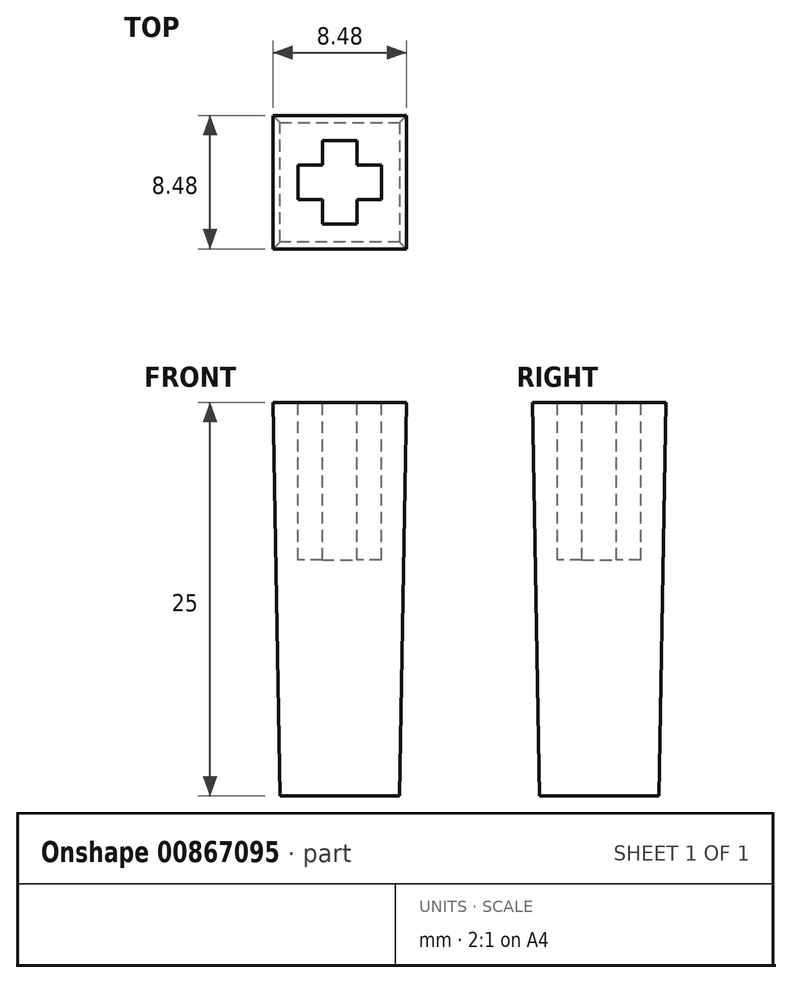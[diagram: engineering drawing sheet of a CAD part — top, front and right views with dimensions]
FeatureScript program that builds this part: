
annotation { "Feature Type Name" : "Feature", "Feature Type Description" : "" }
export const myFeature = defineFeature(function(context is Context, id is Id, definition is map)
    precondition{}
    {
        {
            var Q0;
            Q0=qCreatedBy(makeId("Top.planeOp"),FACE);
            var sketch = newSketch(context, id + "F0", { "sketchPlane" : qUnion([Q0])});
            skLineSegment(sketch, "E0.bottom", {"start": v(3.8, 3.8) * mm, "end": v(-3.8, 3.8) * mm});
            skLineSegment(sketch, "E0.top", {"start": v(3.8, -3.8) * mm, "end": v(-3.8, -3.8) * mm});
            skLineSegment(sketch, "E0.left", {"start": v(3.8, 3.8) * mm, "end": v(3.8, -3.8) * mm});
            skLineSegment(sketch, "E0.right", {"start": v(-3.8, 3.8) * mm, "end": v(-3.8, -3.8) * mm});
            skPoint(sketch, "E0.middle", {"position": v(0, 0) * mm});
            skSolve(sketch);
        }
        {
            var Q0;
            Q0 = qSketchRegion(id + "F0", true);
            extrude(context, id + "F1", {"entities" : qUnion([Q0]), "depth" : 25 * mm, "offsetDistance" : 25 * mm, "hasDraft" : true, "draftAngle" : 1 * degree});
        }
        {
            var Q0;
            Q0=makeQuery(id+"F1.opExtrude","CAP_FACE",FACE,{"disambiguationData":[OSD([sQuery(id+"F0.wireOp",EDGE,"E0.bottom"),sQuery(id+"F0.wireOp",EDGE,"E0.top"),sQuery(id+"F0.wireOp",EDGE,"E0.left"),sQuery(id+"F0.wireOp",EDGE,"E0.right")])],"isStart":false});
            var sketch = newSketch(context, id + "F2", { "sketchPlane" : qUnion([Q0])});
            skLineSegment(sketch, "E1.bottom", {"start": v(2.65, -1.1) * mm, "end": v(-2.65, -1.1) * mm});
            skLineSegment(sketch, "E1.top", {"start": v(2.65, 1.1) * mm, "end": v(-2.65, 1.1) * mm});
            skLineSegment(sketch, "E1.left", {"start": v(2.65, -1.1) * mm, "end": v(2.65, 1.1) * mm});
            skLineSegment(sketch, "E1.right", {"start": v(-2.65, -1.1) * mm, "end": v(-2.65, 1.1) * mm});
            skPoint(sketch, "E1.middle", {"position": v(0, 0) * mm});
            skLineSegment(sketch, "E2.bottom", {"start": v(-1.1, 2.65) * mm, "end": v(1.1, 2.65) * mm});
            skLineSegment(sketch, "E2.top", {"start": v(-1.1, -2.65) * mm, "end": v(1.1, -2.65) * mm});
            skLineSegment(sketch, "E2.left", {"start": v(-1.1, 2.65) * mm, "end": v(-1.1, -2.65) * mm});
            skLineSegment(sketch, "E2.right", {"start": v(1.1, 2.65) * mm, "end": v(1.1, -2.65) * mm});
            skSolve(sketch);
        }
        {
            var Q0;
            Q0 = qSketchRegion(id + "F2", true);
            extrude(context, id + "F3", {"entities" : qUnion([Q0]), "operationType" : NewBodyOperationType.REMOVE, "oppositeDirection" : true, "depth" : 10 * mm, "offsetDistance" : 25 * mm});
        }
    });
